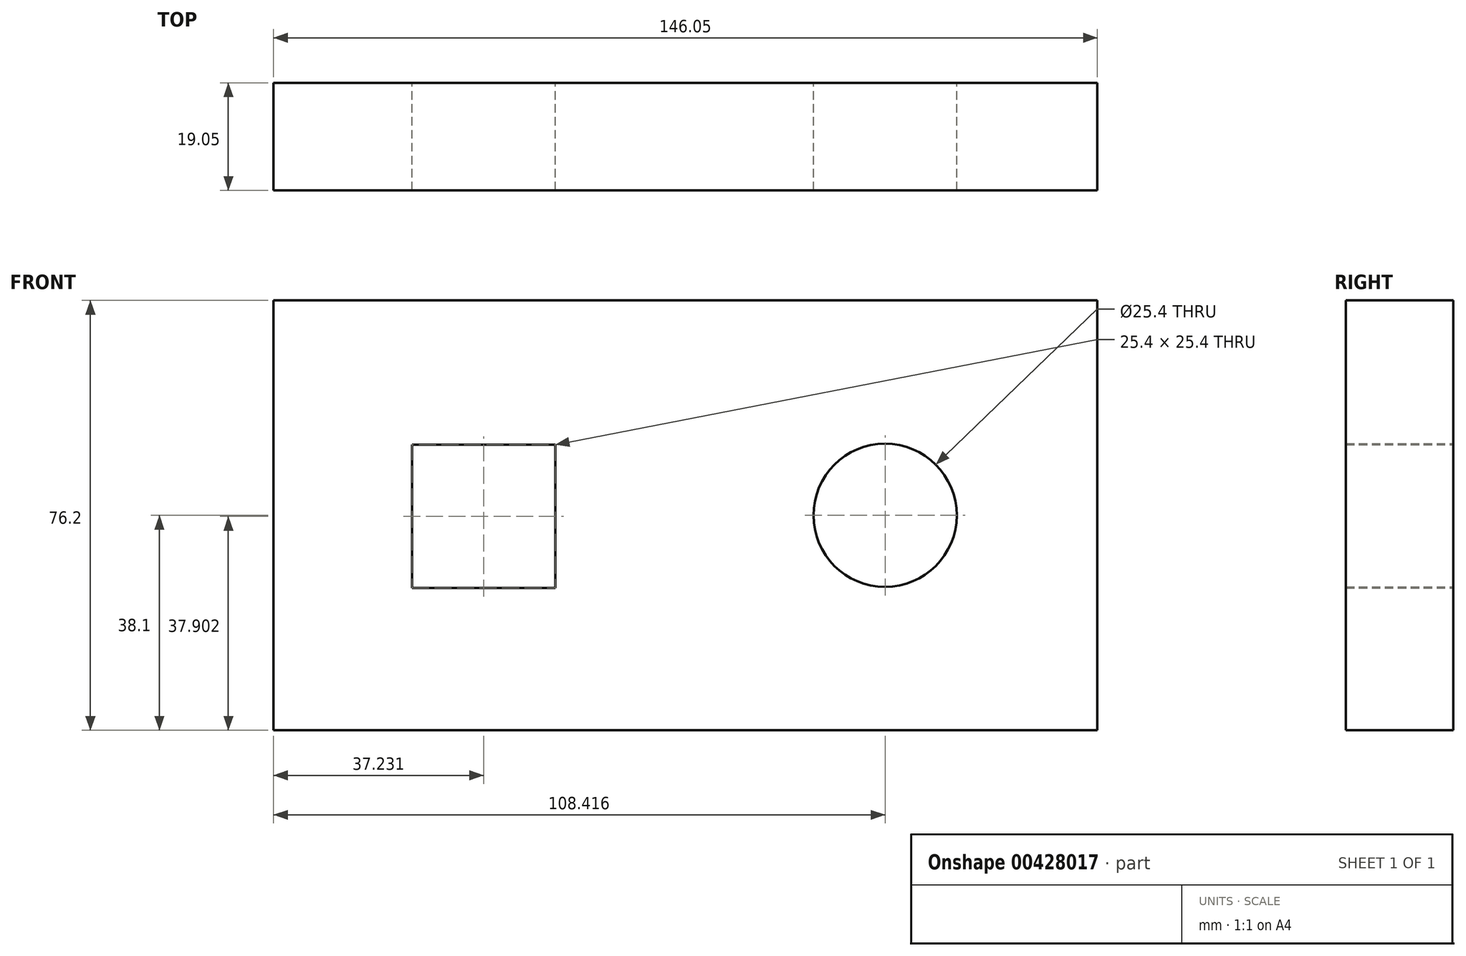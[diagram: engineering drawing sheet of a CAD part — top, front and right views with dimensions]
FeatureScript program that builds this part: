
annotation { "Feature Type Name" : "Feature", "Feature Type Description" : "" }
export const myFeature = defineFeature(function(context is Context, id is Id, definition is map)
    precondition{}
    {
        {
            var Q0;
            Q0=qCreatedBy(makeId("Front.planeOp"),FACE);
            var sketch = newSketch(context, id + "F0", { "sketchPlane" : qUnion([Q0])});
            skLineSegment(sketch, "E0.bottom", {"start": v(0, 0) * mm, "end": v(-146.05, 0) * mm});
            skLineSegment(sketch, "E0.top", {"start": v(0, 76.2) * mm, "end": v(-146.05, 76.2) * mm});
            skLineSegment(sketch, "E0.left", {"start": v(0, 0) * mm, "end": v(0, 76.2) * mm});
            skLineSegment(sketch, "E0.right", {"start": v(-146.05, 0) * mm, "end": v(-146.05, 76.2) * mm});
            skPoint(sketch, "E1.orphan", {"position": v(-146.05, 38.1) * mm});
            skPoint(sketch, "E2.start.orphan", {"position": v(-73.03, 38.1) * mm});
            skPoint(sketch, "E3.start.orphan", {"position": v(-109.54, 38.1) * mm});
            skLineSegment(sketch, "E4", {"start": v(-109.54, 25.2) * mm, "end": v(-109.54, 25.4) * mm});
            skCircle(sketch, "E5", {"center": v(-37.63, 38.1) * mm, "radius": 12.7 * mm});
            skPoint(sketch, "E6.end.orphan", {"position": v(-50.33, 38.1) * mm});
            skPoint(sketch, "E7.end.orphan", {"position": v(0, 38.1) * mm});
            skPoint(sketch, "E7.start.orphan", {"position": v(-24.93, 38.1) * mm});
            skLineSegment(sketch, "E8.bottom", {"start": v(-121.52, 25.2) * mm, "end": v(-96.12, 25.2) * mm});
            skLineSegment(sketch, "E8.top", {"start": v(-121.52, 50.6) * mm, "end": v(-96.12, 50.6) * mm});
            skLineSegment(sketch, "E8.left", {"start": v(-121.52, 25.2) * mm, "end": v(-121.52, 50.6) * mm});
            skLineSegment(sketch, "E8.right", {"start": v(-96.12, 25.2) * mm, "end": v(-96.12, 50.6) * mm});
            skPoint(sketch, "E9.start.orphan", {"position": v(-109.54, 76.2) * mm});
            skPoint(sketch, "E10.orphan", {"position": v(-109.54, 0) * mm});
            skPoint(sketch, "E11.orphan", {"position": v(-73.03, 0) * mm});
            skPoint(sketch, "E12.end.orphan", {"position": v(-73.03, 76.2) * mm});
            skSolve(sketch);
        }
        {
            var Q0;
            Q0=makeQuery(id+"F0.imprint","IMPRINT",FACE,{"disambiguationData":[TD([[makeQuery(id+"F0.imprint","IMPRINT",EDGE,{"derivedFrom":sQuery(id+"F0.wireOp",EDGE,"E0.bottom")}),-1.0]])]});
            extrude(context, id + "F1", {"entities" : qUnion([Q0]), "depth" : 19.05 * mm});
        }
    });
